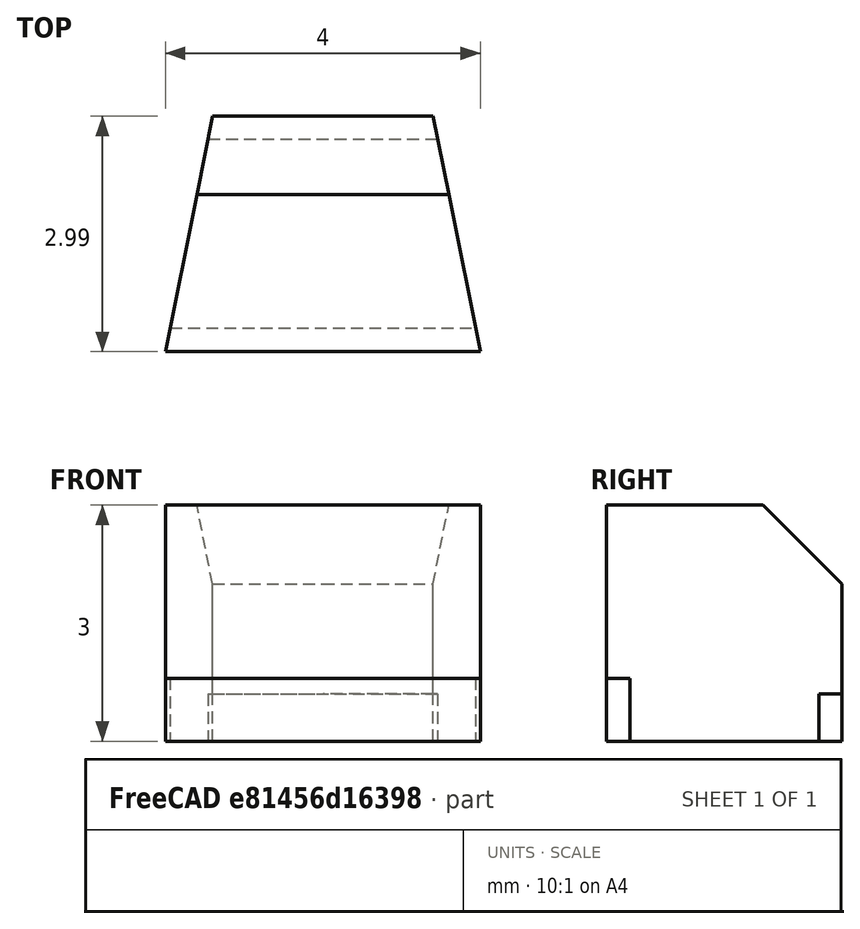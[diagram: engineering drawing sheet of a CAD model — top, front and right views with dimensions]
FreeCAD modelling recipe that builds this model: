
FCSTD DOCUMENT  (FreeCAD 0.18R4 (GitTag))
Label: room_treat
License: All rights reserved
LicenseURL: http://en.wikipedia.org/wiki/All_rights_reserved
objects: Part::Box×2, Part::Cut×2, Sketcher::SketchObject×1, PartDesign::Pad×1, PartDesign::Chamfer×1, PartDesign::Body×1
note: 9 computed .brp shape members not serialized (recipe doc carries the construction recipe); baked Part::Feature solids carry a one-line shape summary decoded from their .brp

FEATURE [Sketcher::SketchObject] Sketch
  MapMode = 5
  Support = -> [XY_Plane]
  sketch-geometry (6):
    g0: LineSegment StartX=0 StartY=0 StartZ=0 EndX=2 EndY=0 EndZ=0
    g1: LineSegment StartX=2 StartY=0 StartZ=0 EndX=1.4 EndY=2.9922 EndZ=0
    g2: LineSegment StartX=1.4 StartY=2.9922 StartZ=0 EndX=0 EndY=2.9922 EndZ=0
    g3: LineSegment StartX=0 StartY=0 StartZ=0 EndX=-2 EndY=0 EndZ=0
    g4: LineSegment StartX=-2 StartY=0 StartZ=0 EndX=-1.4 EndY=2.9922 EndZ=0
    g5: LineSegment StartX=-1.4 StartY=2.9922 StartZ=0 EndX=0 EndY=2.9922 EndZ=0
  constraints (11):
    c: Coincident(g0,g-1)
    c: PointOnObject(g0,g-1)
    c: Coincident(g1,g0)
    c: Coincident(g2,g1)
    c: PointOnObject(g2,g-2)
    c: Horizontal(g2)
    c: DistanceX(g0,g0) = 2
    c: DistanceX(g2,g2) = 1.4
    c: Coincident(g4,g3)
    c: Coincident(g5,g4)
    c: Horizontal(g5)
FEATURE [PartDesign::Pad] Pad
  Length = 3
  Length2 = 100
  Profile = -> Sketch
  Type = 0
FEATURE [PartDesign::Chamfer] Chamfer
  Base = -> Pad [Edge13,Edge10]
  BaseFeature = -> Pad
  Size = 1
FEATURE [PartDesign::Body] Body
  Group = -> [Sketch,Pad,Chamfer]
  Origin = -> Origin
  Tip = -> Chamfer
FEATURE [Part::Box] Box  label="Cube"
  AttacherType = Attacher::AttachEngine3D
  Height = 0.6
  Length = 3
  Placement = pos=(-1.5,2.7,0) rot=(0,0,1;0rad)
  Width = 0.3
FEATURE [Part::Cut] Cut
  Base = -> Chamfer
  Tool = -> Box
FEATURE [Part::Box] Box001  label="Cube001"
  AttacherType = Attacher::AttachEngine3D
  Height = 0.8
  Length = 5
  Placement = pos=(-2.5,0,0) rot=(0,0,1;0rad)
  Width = 0.3
FEATURE [Part::Cut] Cut001
  Base = -> Cut
  Tool = -> Box001
